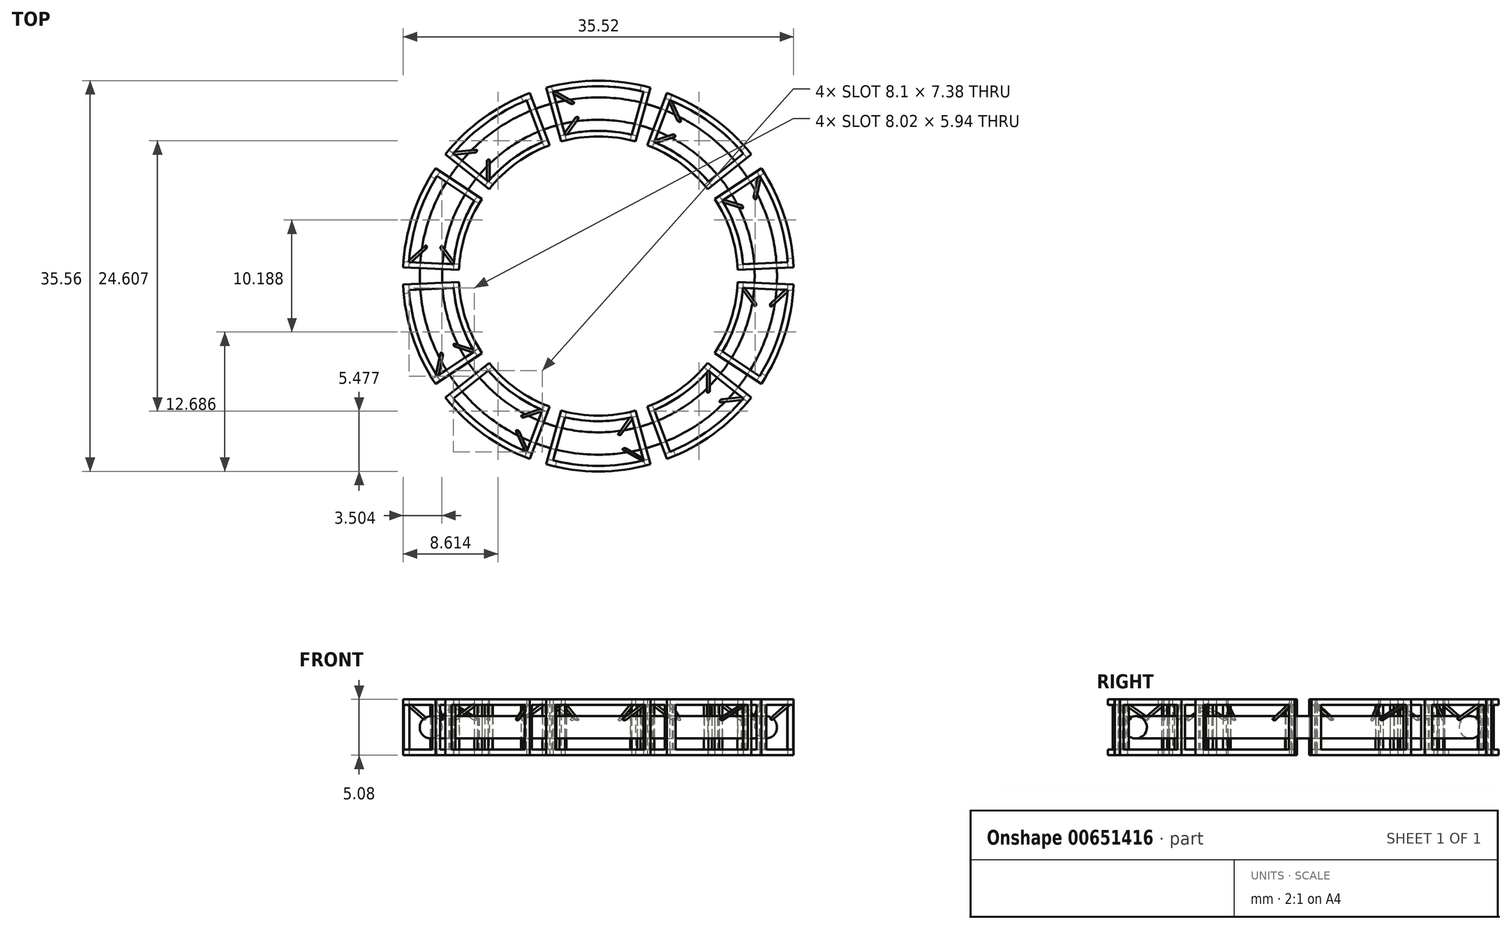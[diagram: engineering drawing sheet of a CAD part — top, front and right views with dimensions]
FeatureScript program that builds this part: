
annotation { "Feature Type Name" : "Feature", "Feature Type Description" : "" }
export const myFeature = defineFeature(function(context is Context, id is Id, definition is map)
    precondition{}
    {
        {
            var Q0;
            Q0=qCreatedBy(makeId("Top.planeOp"),FACE);
            var sketch = newSketch(context, id + "F0", { "sketchPlane" : qUnion([Q0])});
            skArc(sketch, "E0", {"start": v(-4.75, 17.13) * mm, "mid": v(0, 17.78) * mm, "end": v(4.75, 17.13) * mm});
            skArc(sketch, "E1", {"start": v(-3.4, 12.24) * mm, "mid": v(0, 12.7) * mm, "end": v(3.4, 12.24) * mm});
            skLineSegment(sketch, "E2", {"start": v(0, 0) * mm, "end": v(2.72, 9.8) * mm, "construction": true});
            skLineSegment(sketch, "E3", {"start": v(0, 0) * mm, "end": v(-2.72, 9.8) * mm, "construction": true});
            skLineSegment(sketch, "E4", {"start": v(-4.75, 17.13) * mm, "end": v(-3.4, 12.24) * mm});
            skLineSegment(sketch, "E5", {"start": v(4.75, 17.13) * mm, "end": v(3.4, 12.24) * mm});
            skArc(sketch, "E6.0", {"start": v(-4.12, 16.77) * mm, "mid": v(0, 17.27) * mm, "end": v(4.12, 16.77) * mm});
            skArc(sketch, "E7.0", {"start": v(-3.04, 12.85) * mm, "mid": v(0, 13.2) * mm, "end": v(3.04, 12.85) * mm});
            skLineSegment(sketch, "E8.0", {"start": v(4.12, 16.77) * mm, "end": v(3.04, 12.85) * mm});
            skLineSegment(sketch, "E9.0", {"start": v(-4.12, 16.77) * mm, "end": v(-3.04, 12.85) * mm});
            skSolve(sketch);
        }
        {
            var Q0;
            Q0 = qSketchRegion(id + "F0", true);
            extrude(context, id + "F1", {"entities" : qUnion([Q0]), "depth" : 5.08 * mm, "offsetDistance" : 25.4 * mm});
        }
        {
            var Q0;
            Q0=makeQuery(id+"F1.opExtrude","SWEPT_FACE",FACE,{"disambiguationData":[OSD([sQuery(id+"F0.wireOp",EDGE,"E9.0")])]});
            var sketch = newSketch(context, id + "F2", { "sketchPlane" : qUnion([Q0])});
            skLineSegment(sketch, "E10.bottom", {"start": v(12.45, 4.57) * mm, "end": v(18.03, 4.57) * mm});
            skLineSegment(sketch, "E10.top", {"start": v(12.45, 0.5) * mm, "end": v(18.03, 0.5) * mm});
            skLineSegment(sketch, "E10.left", {"start": v(12.45, 4.57) * mm, "end": v(12.45, 0.5) * mm});
            skLineSegment(sketch, "E10.right", {"start": v(18.03, 4.57) * mm, "end": v(18.03, 0.5) * mm});
            skSolve(sketch);
        }
        {
            var Q0;
            Q0 = qSketchRegion(id + "F2", true);
            var Q1;
            Q1=makeQuery(id+"F1.opExtrude","CAP_EDGE",EDGE,{"disambiguationData":[OSD([sQuery(id+"F0.wireOp",EDGE,"E7.0")])],"isStart":false});
            sweep(context, id + "F3", {"operationType" : NewBodyOperationType.REMOVE, "profiles" : qUnion([Q0]), "path" : qUnion([Q1])});
        }
        {
            var Q0;
            Q0=makeQuery(id+"F1.opExtrude","SWEPT_FACE",FACE,{"disambiguationData":[OSD([sQuery(id+"F0.wireOp",EDGE,"E5")])]});
            var sketch = newSketch(context, id + "F4", { "sketchPlane" : qUnion([Q0])});
            skLineSegment(sketch, "E11.bottom", {"start": v(13.2, 4.57) * mm, "end": v(17.27, 4.57) * mm});
            skLineSegment(sketch, "E11.top", {"start": v(13.2, 0.5) * mm, "end": v(17.27, 0.5) * mm});
            skLineSegment(sketch, "E11.left", {"start": v(13.2, 4.57) * mm, "end": v(13.2, 0.5) * mm});
            skLineSegment(sketch, "E11.right", {"start": v(17.27, 4.57) * mm, "end": v(17.27, 0.5) * mm});
            skSolve(sketch);
        }
        {
            var Q0;
            Q0 = qSketchRegion(id + "F4", true);
            var Q1;
            Q1=makeQuery(id+"F1.opExtrude","CAP_EDGE",EDGE,{"disambiguationData":[OSD([sQuery(id+"F0.wireOp",EDGE,"E1")])],"isStart":false});
            sweep(context, id + "F5", {"operationType" : NewBodyOperationType.REMOVE, "profiles" : qUnion([Q0]), "path" : qUnion([Q1])});
        }
        {
            var Q0;
            Q0=qCreatedBy(makeId("Top.planeOp"),FACE);
            cPlane(context, id + "F6", {"entities" : qUnion([Q0]), "cplaneType" : CPlaneType.OFFSET, "offset" : 2.54 * mm, "width" : 152.4 * mm, "height" : 152.4 * mm});
        }
        {
            var Q0;
            Q0=qCreatedBy(id+"F6.planeOp",FACE);
            var sketch = newSketch(context, id + "F7", { "sketchPlane" : qUnion([Q0])});
            skArc(sketch, "E12", {"start": v(-4.07, 14.69) * mm, "mid": v(0, 15.24) * mm, "end": v(4.07, 14.69) * mm});
            skLineSegment(sketch, "E13", {"start": v(0, 0) * mm, "end": v(-1.37, 15.18) * mm});
            skLineSegment(sketch, "E14", {"start": v(0, 0) * mm, "end": v(1.37, 15.18) * mm});
            skSolve(sketch);
        }
        {
            var Q0;
            Q0=makeQuery(id+"F3.boolean.opBoolean","INTERSECT",VERTEX,{"derivedFrom":[makeQuery(id+"F1.opExtrude","SWEPT_FACE",FACE,{"disambiguationData":[OSD([sQuery(id+"F0.wireOp",EDGE,"E6.0")])]}),makeQuery(id+"F3.opSweep","SWEPT_FACE",FACE,{"disambiguationData":[OSD([sQuery(id+"F0.wireOp",EDGE,"E7.0"),sQuery(id+"F2.wireOp",EDGE,"E10.bottom")])]})]});
            var Q1;
            Q1=sQuery(id+"F7.wireOp",VERTEX,"E13.end");
            var Q2;
            {var subQ0=sQuery(id+"F0.wireOp",EDGE,"E7.0");Q2=makeQuery(id+"F3.boolean.opBoolean","INTERSECT",VERTEX,{"disambiguationData":[OD(0.0)],"derivedFrom":[makeQuery(id+"F1.opExtrude","SWEPT_FACE",FACE,{"disambiguationData":[OSD([subQ0])]}),makeQuery(id+"F3.opSweep","SWEPT_FACE",FACE,{"disambiguationData":[OSD([subQ0,sQuery(id+"F2.wireOp",EDGE,"E10.bottom")])]})]});}
            cPlane(context, id + "F8", {"entities" : qUnion([Q0, Q1, Q2]), "cplaneType" : CPlaneType.THREE_POINT, "offset" : 25.4 * mm, "width" : 152.4 * mm, "height" : 152.4 * mm});
        }
        {
            var Q0;
            Q0=qCreatedBy(id+"F8.planeOp",FACE);
            var sketch = newSketch(context, id + "F9", { "sketchPlane" : qUnion([Q0])});
            skLineSegment(sketch, "E15", {"start": v(-8.6, 15.21) * mm, "end": v(-4.98, 14.14) * mm});
            skLineSegment(sketch, "E16", {"start": v(-7.17, 11.4) * mm, "end": v(-4.98, 14.14) * mm});
            skSolve(sketch);
        }
        {
            var Q0;
            Q0=sQuery(id+"F9.wireOp",VERTEX,"E15.end");
            var Q1;
            Q1=sQuery(id+"F9.wireOp",EDGE,"E16");
            cPlane(context, id + "F10", {"entities" : qUnion([Q0, Q1]), "cplaneType" : CPlaneType.LINE_POINT, "offset" : 25.4 * mm, "width" : 152.4 * mm, "height" : 152.4 * mm});
        }
        {
            var Q0;
            Q0=qCreatedBy(id+"F10.planeOp",FACE);
            var sketch = newSketch(context, id + "F11", { "sketchPlane" : qUnion([Q0])});
            skCircle(sketch, "E17", {"center": v(5.84, 11.9) * mm, "radius": 0.13 * mm});
            skSolve(sketch);
        }
        {
            var Q0;
            Q0 = qSketchRegion(id + "F11", true);
            var Q1;
            Q1 = qConstructionFilter(qBodyType(qCreatedBy(id + "F11" ,EDGE), BodyType.WIRE), ConstructionObject.NO);
            extrude(context, id + "F12", {"entities" : qUnion([Q0]), "operationType" : NewBodyOperationType.ADD, "surfaceEntities" : qUnion([Q1]), "oppositeDirection" : true, "depth" : 4.06 * mm, "offsetDistance" : 25.4 * mm});
        }
        {
            var Q0;
            Q0=sQuery(id+"F9.wireOp",VERTEX,"E16.end");
            var Q1;
            Q1=sQuery(id+"F9.wireOp",EDGE,"E15");
            cPlane(context, id + "F13", {"entities" : qUnion([Q0, Q1]), "cplaneType" : CPlaneType.LINE_POINT, "offset" : 25.4 * mm, "width" : 152.4 * mm, "height" : 152.4 * mm});
        }
        {
            var Q0;
            Q0=qCreatedBy(id+"F13.planeOp",FACE);
            var sketch = newSketch(context, id + "F14", { "sketchPlane" : qUnion([Q0])});
            skCircle(sketch, "E18", {"center": v(12.65, 1.23) * mm, "radius": 0.13 * mm});
            skSolve(sketch);
        }
        {
            var Q0;
            Q0 = qSketchRegion(id + "F14", true);
            var Q1;
            Q1=makeQuery(id+"F1.opExtrude","CAP_VERTEX",VERTEX,{"disambiguationData":[OSD([sQuery(id+"F0.wireOp",EDGE,"E0"),sQuery(id+"F0.wireOp",EDGE,"E4")])],"isStart":false});
            extrude(context, id + "F15", {"entities" : qUnion([Q0]), "operationType" : NewBodyOperationType.ADD, "oppositeDirection" : true, "depth" : 4.37 * mm, "endBoundEntityVertex" : qUnion([Q1]), "hasOffset" : true, "offsetDistance" : 0.25 * mm});
        }
        {
            var Q0;
            Q0=qCreatedBy(id+"F6.planeOp",FACE);
            var sketch = newSketch(context, id + "F16", { "sketchPlane" : qUnion([Q0])});
            skLineSegment(sketch, "E19.bottom", {"start": v(-2.17, 15.6) * mm, "end": v(-0.81, 15.6) * mm});
            skLineSegment(sketch, "E19.top", {"start": v(-2.17, 14.74) * mm, "end": v(-0.81, 14.74) * mm});
            skLineSegment(sketch, "E19.left", {"start": v(-2.17, 15.6) * mm, "end": v(-2.17, 14.74) * mm});
            skLineSegment(sketch, "E19.right", {"start": v(-0.81, 15.6) * mm, "end": v(-0.81, 14.74) * mm});
            skSolve(sketch);
        }
        {
            var Q0;
            Q0=makeQuery(id+"F16.imprint","IMPRINT",FACE,{"disambiguationData":[TD([[makeQuery(id+"F16.imprint","IMPRINT",EDGE,{"derivedFrom":sQuery(id+"F16.wireOp",EDGE,"E19.bottom")}),-1.0]])]});
            extrude(context, id + "F17", {"entities" : qUnion([Q0]), "operationType" : NewBodyOperationType.REMOVE, "oppositeDirection" : true, "depth" : 25.4 * mm, "offsetDistance" : 25.4 * mm});
        }
        {
            var Q0;
            Q0=makeQuery(id+"F1.opExtrude","SWEPT_BODY",BODY,{"disambiguationData":[OSD([sQuery(id+"F0.wireOp",EDGE,"E0"),sQuery(id+"F0.wireOp",EDGE,"E1"),sQuery(id+"F0.wireOp",EDGE,"E4"),sQuery(id+"F0.wireOp",EDGE,"E5"),sQuery(id+"F0.wireOp",EDGE,"E6.0"),sQuery(id+"F0.wireOp",EDGE,"E7.0"),sQuery(id+"F0.wireOp",EDGE,"E8.0"),sQuery(id+"F0.wireOp",EDGE,"E9.0")])]});
            var Q1;
            Q1=makeQuery(id+"F1.opExtrude","SWEPT_FACE",FACE,{"disambiguationData":[OSD([sQuery(id+"F0.wireOp",EDGE,"E1")])]});
            circularPattern(context, id + "F18", {"entities" : qUnion([Q0]), "axis" : qUnion([Q1]), "angle" : 360 * degree, "instanceCount" : 10, "equalSpace" : true});
        }
        {
            var Q0;
            Q0=makeQuery(id+"F1.opExtrude","SWEPT_FACE",FACE,{"disambiguationData":[OSD([sQuery(id+"F0.wireOp",EDGE,"E5")])]});
            var sketch = newSketch(context, id + "F19", { "sketchPlane" : qUnion([Q0])});
            skCircle(sketch, "E20", {"center": v(15.24, 2.54) * mm, "radius": 1.02 * mm});
            skSolve(sketch);
        }
        {
            var Q0;
            Q0=qCreatedBy(id+"F6.planeOp",FACE);
            var sketch = newSketch(context, id + "F20", { "sketchPlane" : qUnion([Q0])});
            skCircle(sketch, "E21", {"center": v(0, 0) * mm, "radius": 15.24 * mm});
            skSolve(sketch);
        }
        {
            var Q0;
            Q0 = qSketchRegion(id + "F19", true);
            var Q1;
            Q1 = qConstructionFilter(qBodyType(qCreatedBy(id + "F20" ,EDGE), BodyType.WIRE), ConstructionObject.NO);
            sweep(context, id + "F21", {"operationType" : NewBodyOperationType.ADD, "profiles" : qUnion([Q0]), "path" : qUnion([Q1])});
        }
    });
